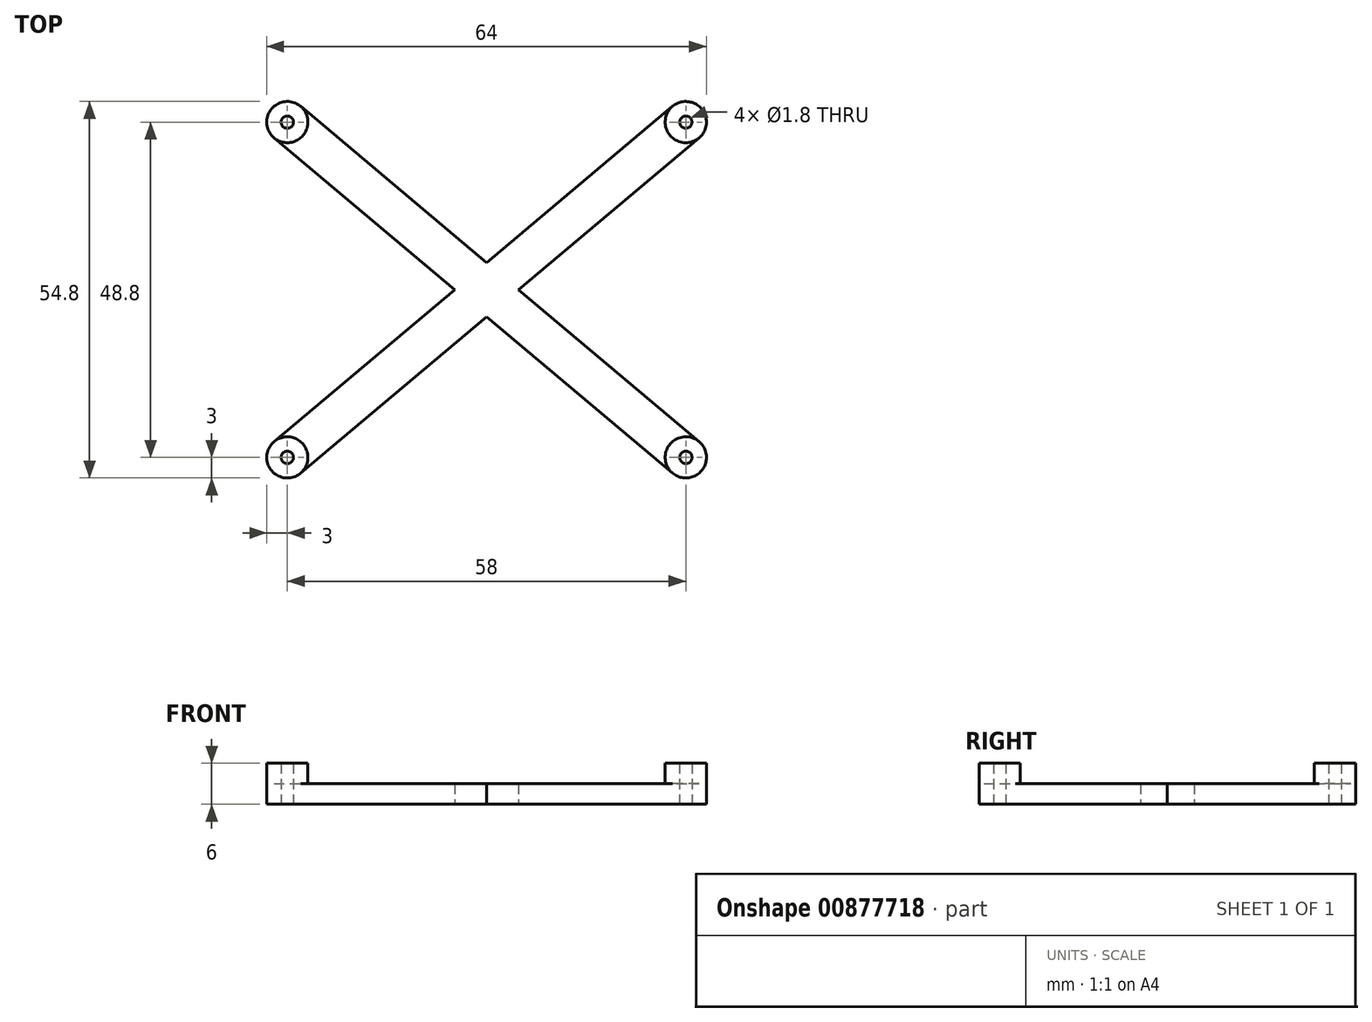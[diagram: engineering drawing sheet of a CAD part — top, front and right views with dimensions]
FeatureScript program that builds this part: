
annotation { "Feature Type Name" : "Feature", "Feature Type Description" : "" }
export const myFeature = defineFeature(function(context is Context, id is Id, definition is map)
    precondition{}
    {
        {
            var Q0;
            Q0=qCreatedBy(makeId("Top.planeOp"),FACE);
            var sketch = newSketch(context, id + "F0", { "sketchPlane" : qUnion([Q0])});
            skPoint(sketch, "E0", {"position": v(-29, 24.4) * mm});
            skPoint(sketch, "E1", {"position": v(29, 24.4) * mm});
            skPoint(sketch, "E2", {"position": v(29, -24.4) * mm});
            skPoint(sketch, "E3", {"position": v(-29, -24.4) * mm});
            skLineSegment(sketch, "E4", {"start": v(-29, 24.4) * mm, "end": v(29, -24.4) * mm});
            skLineSegment(sketch, "E5", {"start": v(-29, -24.4) * mm, "end": v(29, 24.4) * mm});
            skArc(sketch, "E6.0.startCap", {"start": v(-27.07, -26.7) * mm, "mid": v(-31.3, -26.33) * mm, "end": v(-30.93, -22.1) * mm});
            skArc(sketch, "E6.0.endCap", {"start": v(27.07, 26.7) * mm, "mid": v(31.3, 26.33) * mm, "end": v(30.93, 22.1) * mm});
            skLineSegment(sketch, "E6.0.left", {"start": v(-30.93, -22.1) * mm, "end": v(27.07, 26.7) * mm});
            skLineSegment(sketch, "E6.0.right", {"start": v(-27.07, -26.7) * mm, "end": v(30.93, 22.1) * mm});
            skArc(sketch, "E6.1.startCap", {"start": v(-30.93, 22.1) * mm, "mid": v(-31.3, 26.33) * mm, "end": v(-27.07, 26.7) * mm});
            skArc(sketch, "E6.1.endCap", {"start": v(30.93, -22.1) * mm, "mid": v(31.3, -26.33) * mm, "end": v(27.07, -26.7) * mm});
            skLineSegment(sketch, "E6.1.left", {"start": v(-27.07, 26.7) * mm, "end": v(30.93, -22.1) * mm});
            skLineSegment(sketch, "E6.1.right", {"start": v(-30.93, 22.1) * mm, "end": v(27.07, -26.7) * mm});
            skCircle(sketch, "E7", {"center": v(-29, 24.4) * mm, "radius": 0.9 * mm});
            skCircle(sketch, "E8", {"center": v(29, 24.4) * mm, "radius": 0.9 * mm});
            skCircle(sketch, "E9", {"center": v(29, -24.4) * mm, "radius": 0.9 * mm});
            skCircle(sketch, "E10", {"center": v(-29, -24.4) * mm, "radius": 0.9 * mm});
            skCircle(sketch, "E11", {"center": v(-29, 24.4) * mm, "radius": 3 * mm});
            skCircle(sketch, "E12", {"center": v(29, 24.4) * mm, "radius": 3 * mm});
            skCircle(sketch, "E13", {"center": v(29, -24.4) * mm, "radius": 3 * mm});
            skCircle(sketch, "E14", {"center": v(-29, -24.4) * mm, "radius": 3 * mm});
            skSolve(sketch);
        }
        {
            var Q0;
            {var subQ0=sQuery(id+"F0.wireOp",EDGE,"E11");var subQ1=sQuery(id+"F0.wireOp",EDGE,"E4");var subQ2=makeQuery(id+"F0.imprint","INTERSECT",VERTEX,{"derivedFrom":[subQ1,subQ0]});Q0=makeQuery(id+"F0.imprint","IMPRINT",FACE,{"disambiguationData":[TD([[makeQuery(id+"F0.imprint","IMPRINT",EDGE,{"disambiguationData":[TD([[subQ2,-1.0]])],"derivedFrom":subQ1}),1.0]])]});}
            var Q1;
            {var subQ0=sQuery(id+"F0.wireOp",EDGE,"E11");var subQ1=sQuery(id+"F0.wireOp",EDGE,"E4");var subQ2=makeQuery(id+"F0.imprint","INTERSECT",VERTEX,{"derivedFrom":[subQ1,subQ0]});Q1=makeQuery(id+"F0.imprint","IMPRINT",FACE,{"disambiguationData":[TD([[makeQuery(id+"F0.imprint","IMPRINT",EDGE,{"disambiguationData":[TD([[subQ2,-1.0]])],"derivedFrom":subQ1}),-1.0]])]});}
            var Q2;
            {var subQ0=sQuery(id+"F0.wireOp",EDGE,"E12");var subQ1=sQuery(id+"F0.wireOp",EDGE,"E5");var subQ2=makeQuery(id+"F0.imprint","INTERSECT",VERTEX,{"derivedFrom":[subQ1,subQ0]});Q2=makeQuery(id+"F0.imprint","IMPRINT",FACE,{"disambiguationData":[TD([[makeQuery(id+"F0.imprint","IMPRINT",EDGE,{"disambiguationData":[TD([[subQ2,1.0]])],"derivedFrom":subQ1}),1.0]])]});}
            var Q3;
            {var subQ0=sQuery(id+"F0.wireOp",EDGE,"E12");var subQ1=sQuery(id+"F0.wireOp",EDGE,"E5");var subQ2=makeQuery(id+"F0.imprint","INTERSECT",VERTEX,{"derivedFrom":[subQ1,subQ0]});Q3=makeQuery(id+"F0.imprint","IMPRINT",FACE,{"disambiguationData":[TD([[makeQuery(id+"F0.imprint","IMPRINT",EDGE,{"disambiguationData":[TD([[subQ2,1.0]])],"derivedFrom":subQ1}),-1.0]])]});}
            var Q4;
            {var subQ0=sQuery(id+"F0.wireOp",EDGE,"E6.0.left");var subQ1=sQuery(id+"F0.wireOp",EDGE,"E4");var subQ2=makeQuery(id+"F0.imprint","INTERSECT",VERTEX,{"derivedFrom":[subQ1,subQ0]});Q4=makeQuery(id+"F0.imprint","IMPRINT",FACE,{"disambiguationData":[TD([[makeQuery(id+"F0.imprint","IMPRINT",EDGE,{"disambiguationData":[TD([[subQ2,-1.0]])],"derivedFrom":subQ1}),1.0]])]});}
            var Q5;
            {var subQ0=sQuery(id+"F0.wireOp",EDGE,"E6.0.left");var subQ1=sQuery(id+"F0.wireOp",EDGE,"E4");var subQ2=makeQuery(id+"F0.imprint","INTERSECT",VERTEX,{"derivedFrom":[subQ1,subQ0]});Q5=makeQuery(id+"F0.imprint","IMPRINT",FACE,{"disambiguationData":[TD([[makeQuery(id+"F0.imprint","IMPRINT",EDGE,{"disambiguationData":[TD([[subQ2,-1.0]])],"derivedFrom":subQ1}),-1.0]])]});}
            var Q6;
            {var subQ0=sQuery(id+"F0.wireOp",EDGE,"E5");var subQ1=sQuery(id+"F0.wireOp",EDGE,"E4");var subQ2=makeQuery(id+"F0.imprint","INTERSECT",VERTEX,{"derivedFrom":[subQ1,subQ0]});Q6=makeQuery(id+"F0.imprint","IMPRINT",FACE,{"disambiguationData":[TD([[makeQuery(id+"F0.imprint","IMPRINT",EDGE,{"disambiguationData":[TD([[subQ2,-1.0]])],"derivedFrom":subQ1}),1.0]])]});}
            var Q7;
            {var subQ0=sQuery(id+"F0.wireOp",EDGE,"E5");var subQ1=sQuery(id+"F0.wireOp",EDGE,"E4");var subQ2=makeQuery(id+"F0.imprint","INTERSECT",VERTEX,{"derivedFrom":[subQ1,subQ0]});Q7=makeQuery(id+"F0.imprint","IMPRINT",FACE,{"disambiguationData":[TD([[makeQuery(id+"F0.imprint","IMPRINT",EDGE,{"disambiguationData":[TD([[subQ2,-1.0]])],"derivedFrom":subQ1}),-1.0]])]});}
            var Q8;
            {var subQ0=sQuery(id+"F0.wireOp",EDGE,"E14");var subQ1=sQuery(id+"F0.wireOp",EDGE,"E5");var subQ2=makeQuery(id+"F0.imprint","INTERSECT",VERTEX,{"derivedFrom":[subQ1,subQ0]});Q8=makeQuery(id+"F0.imprint","IMPRINT",FACE,{"disambiguationData":[TD([[makeQuery(id+"F0.imprint","IMPRINT",EDGE,{"disambiguationData":[TD([[subQ2,-1.0]])],"derivedFrom":subQ1}),1.0]])]});}
            var Q9;
            {var subQ0=sQuery(id+"F0.wireOp",EDGE,"E14");var subQ1=sQuery(id+"F0.wireOp",EDGE,"E5");var subQ2=makeQuery(id+"F0.imprint","INTERSECT",VERTEX,{"derivedFrom":[subQ1,subQ0]});Q9=makeQuery(id+"F0.imprint","IMPRINT",FACE,{"disambiguationData":[TD([[makeQuery(id+"F0.imprint","IMPRINT",EDGE,{"disambiguationData":[TD([[subQ2,-1.0]])],"derivedFrom":subQ1}),-1.0]])]});}
            var Q10;
            {var subQ0=sQuery(id+"F0.wireOp",EDGE,"E13");var subQ1=sQuery(id+"F0.wireOp",EDGE,"E4");var subQ2=makeQuery(id+"F0.imprint","INTERSECT",VERTEX,{"derivedFrom":[subQ1,subQ0]});Q10=makeQuery(id+"F0.imprint","IMPRINT",FACE,{"disambiguationData":[TD([[makeQuery(id+"F0.imprint","IMPRINT",EDGE,{"disambiguationData":[TD([[subQ2,1.0]])],"derivedFrom":subQ1}),1.0]])]});}
            var Q11;
            {var subQ0=sQuery(id+"F0.wireOp",EDGE,"E13");var subQ1=sQuery(id+"F0.wireOp",EDGE,"E4");var subQ2=makeQuery(id+"F0.imprint","INTERSECT",VERTEX,{"derivedFrom":[subQ1,subQ0]});Q11=makeQuery(id+"F0.imprint","IMPRINT",FACE,{"disambiguationData":[TD([[makeQuery(id+"F0.imprint","IMPRINT",EDGE,{"disambiguationData":[TD([[subQ2,1.0]])],"derivedFrom":subQ1}),-1.0]])]});}
            extrude(context, id + "F1", {"entities" : qUnion([Q0, Q1, Q2, Q3, Q4, Q5, Q6, Q7, Q8, Q9, Q10, Q11]), "depth" : 3 * mm, "offsetDistance" : 25 * mm});
        }
        {
            var Q0;
            Q0=makeQuery(id+"F0.imprint","IMPRINT",FACE,{"disambiguationData":[TD([[makeQuery(id+"F0.imprint","IMPRINT",EDGE,{"derivedFrom":sQuery(id+"F0.wireOp",EDGE,"E7")}),-1.0]])]});
            var Q1;
            Q1=makeQuery(id+"F0.imprint","IMPRINT",FACE,{"disambiguationData":[TD([[makeQuery(id+"F0.imprint","IMPRINT",EDGE,{"derivedFrom":sQuery(id+"F0.wireOp",EDGE,"E8")}),-1.0]])]});
            var Q2;
            Q2=makeQuery(id+"F0.imprint","IMPRINT",FACE,{"disambiguationData":[TD([[makeQuery(id+"F0.imprint","IMPRINT",EDGE,{"derivedFrom":sQuery(id+"F0.wireOp",EDGE,"E9")}),-1.0]])]});
            var Q3;
            Q3=makeQuery(id+"F0.imprint","IMPRINT",FACE,{"disambiguationData":[TD([[makeQuery(id+"F0.imprint","IMPRINT",EDGE,{"derivedFrom":sQuery(id+"F0.wireOp",EDGE,"E10")}),-1.0]])]});
            extrude(context, id + "F2", {"entities" : qUnion([Q0, Q1, Q2, Q3]), "operationType" : NewBodyOperationType.ADD, "depth" : 6 * mm, "offsetDistance" : 25 * mm});
        }
    });
